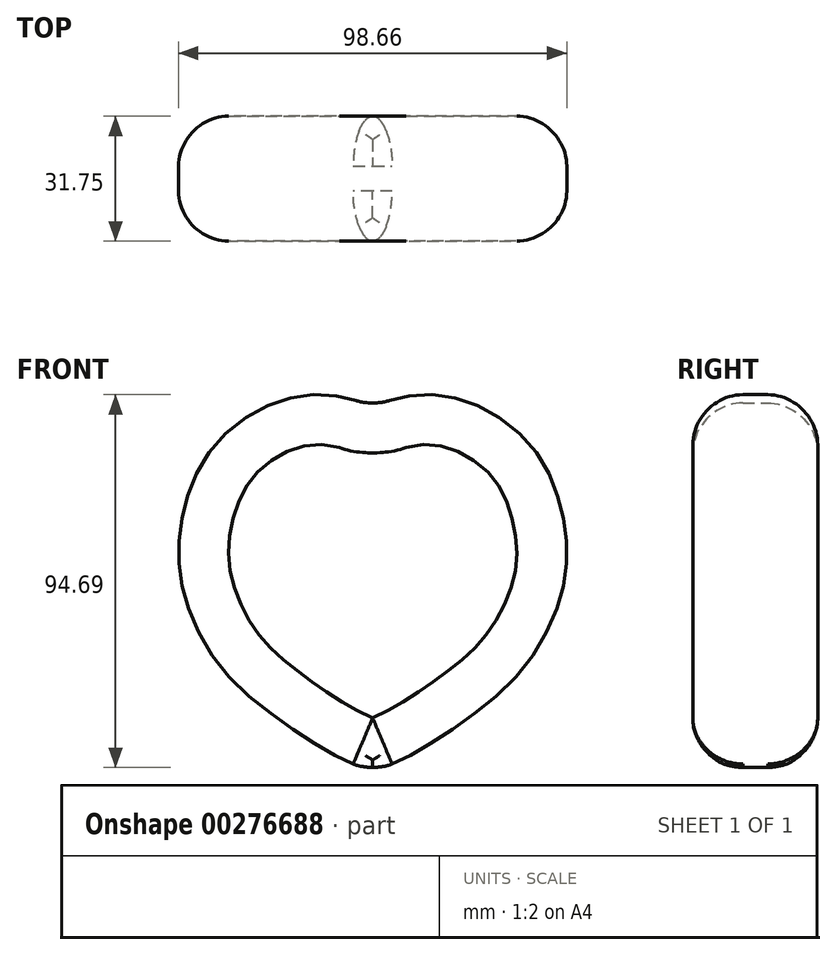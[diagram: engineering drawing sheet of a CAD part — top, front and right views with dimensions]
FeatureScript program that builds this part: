
annotation { "Feature Type Name" : "Feature", "Feature Type Description" : "" }
export const myFeature = defineFeature(function(context is Context, id is Id, definition is map)
    precondition{}
    {
        {
            var Q0;
            Q0=qCreatedBy(makeId("Front.planeOp"),FACE);
            var sketch = newSketch(context, id + "F0", { "sketchPlane" : qUnion([Q0])});
            skFitSpline(sketch, "E0", {"points": [v(0, 0) * mm, v(8.76, 3.7) * mm, v(22.35, 12.25) * mm, v(37.48, 25.18) * mm, v(46.69, 41.19) * mm, v(49.32, 54.78) * mm, v(47.56, 68.16) * mm, v(40.99, 81.97) * mm, v(27.83, 92.5) * mm, v(14.02, 95.78) * mm, v(3.06, 93.8) * mm, v(0, 91.61) * mm], "startDerivative": vector(109.87, 40.83) * mm, "endDerivative": vector(-50.63, -47.67) * mm});
            skFitSpline(sketch, "E1.MirrorCS", {"points": [v(0, 0) * mm, v(-8.76, 3.7) * mm, v(-22.35, 12.25) * mm, v(-37.48, 25.18) * mm, v(-46.69, 41.19) * mm, v(-49.32, 54.78) * mm, v(-47.56, 68.16) * mm, v(-40.99, 81.97) * mm, v(-27.83, 92.5) * mm, v(-14.02, 95.78) * mm, v(-3.06, 93.8) * mm, v(0, 91.61) * mm], "startDerivative": vector(-109.87, 40.83) * mm, "endDerivative": vector(50.63, -47.67) * mm});
            skSolve(sketch);
        }
        {
            var Q0;
            Q0=qSketchRegion(id+"F0",true);
            extrude(context, id + "F1", {"entities" : qUnion([Q0]), "depth" : 31.75 * mm, "offsetDistance" : 25.4 * mm});
        }
        {
            var Q0;
            Q0=makeQuery(id+"F1.opExtrude","CAP_FACE",FACE,{"disambiguationData":[OSD([sQuery(id+"F0.wireOp",EDGE,"E0"),sQuery(id+"F0.wireOp",EDGE,"E1.MirrorCS")])],"isStart":false});
            var Q1;
            Q1=makeQuery(id+"F1.opExtrude","SWEPT_FACE",FACE,{"disambiguationData":[OSD([sQuery(id+"F0.wireOp",EDGE,"E1.MirrorCS")])]});
            var Q2;
            Q2=makeQuery(id+"F1.opExtrude","CAP_EDGE",EDGE,{"disambiguationData":[OSD([sQuery(id+"F0.wireOp",EDGE,"E1.MirrorCS")])],"isStart":false});
            var Q3;
            Q3=makeQuery(id+"F1.opExtrude","SWEPT_FACE",FACE,{"disambiguationData":[OSD([sQuery(id+"F0.wireOp",EDGE,"E0")])]});
            var Q4;
            Q4=makeQuery(id+"F1.opExtrude","CAP_EDGE",EDGE,{"disambiguationData":[OSD([sQuery(id+"F0.wireOp",EDGE,"E0")])],"isStart":false});
            fillet(context, id + "F2", {"entities" : qUnion([Q0, Q1, Q2, Q3, Q4]), "radius" : 12.7 * mm, "rho" : 0.4, "crossSection" : FilletCrossSection.CONIC, "allowEdgeOverflow" : false});
        }
    });
